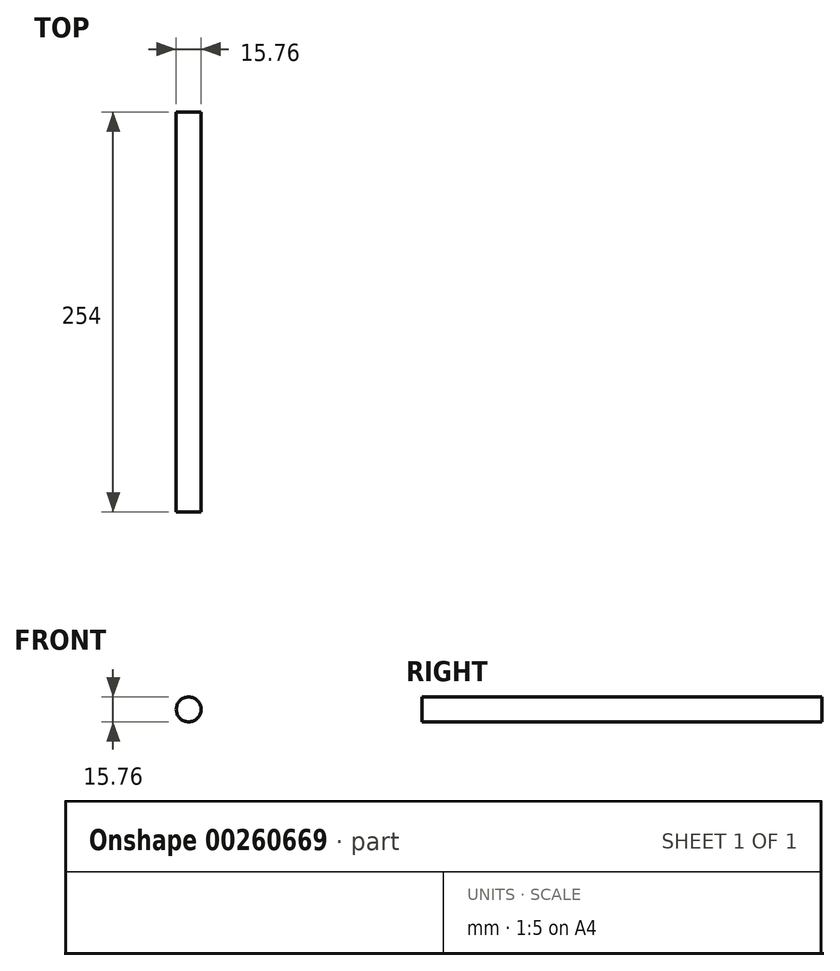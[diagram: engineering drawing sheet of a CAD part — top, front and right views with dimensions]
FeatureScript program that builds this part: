
annotation { "Feature Type Name" : "Feature", "Feature Type Description" : "" }
export const myFeature = defineFeature(function(context is Context, id is Id, definition is map)
    precondition{}
    {
        {
            var Q0;
            Q0=qCreatedBy(makeId("Front.planeOp"),FACE);
            var sketch = newSketch(context, id + "F0", { "sketchPlane" : qUnion([Q0])});
            skCircle(sketch, "E0", {"center": v(-35.16, 22.44) * mm, "radius": 7.88 * mm});
            skSolve(sketch);
        }
        {
            var Q0;
            Q0=makeQuery(id+"F0.imprint","IMPRINT",FACE,{"disambiguationData":[TD([[makeQuery(id+"F0.imprint","IMPRINT",EDGE,{"derivedFrom":sQuery(id+"F0.wireOp",EDGE,"E0")}),1.0]])]});
            extrude(context, id + "F1", {"entities" : qUnion([Q0]), "depth" : 254 * mm});
        }
    });
